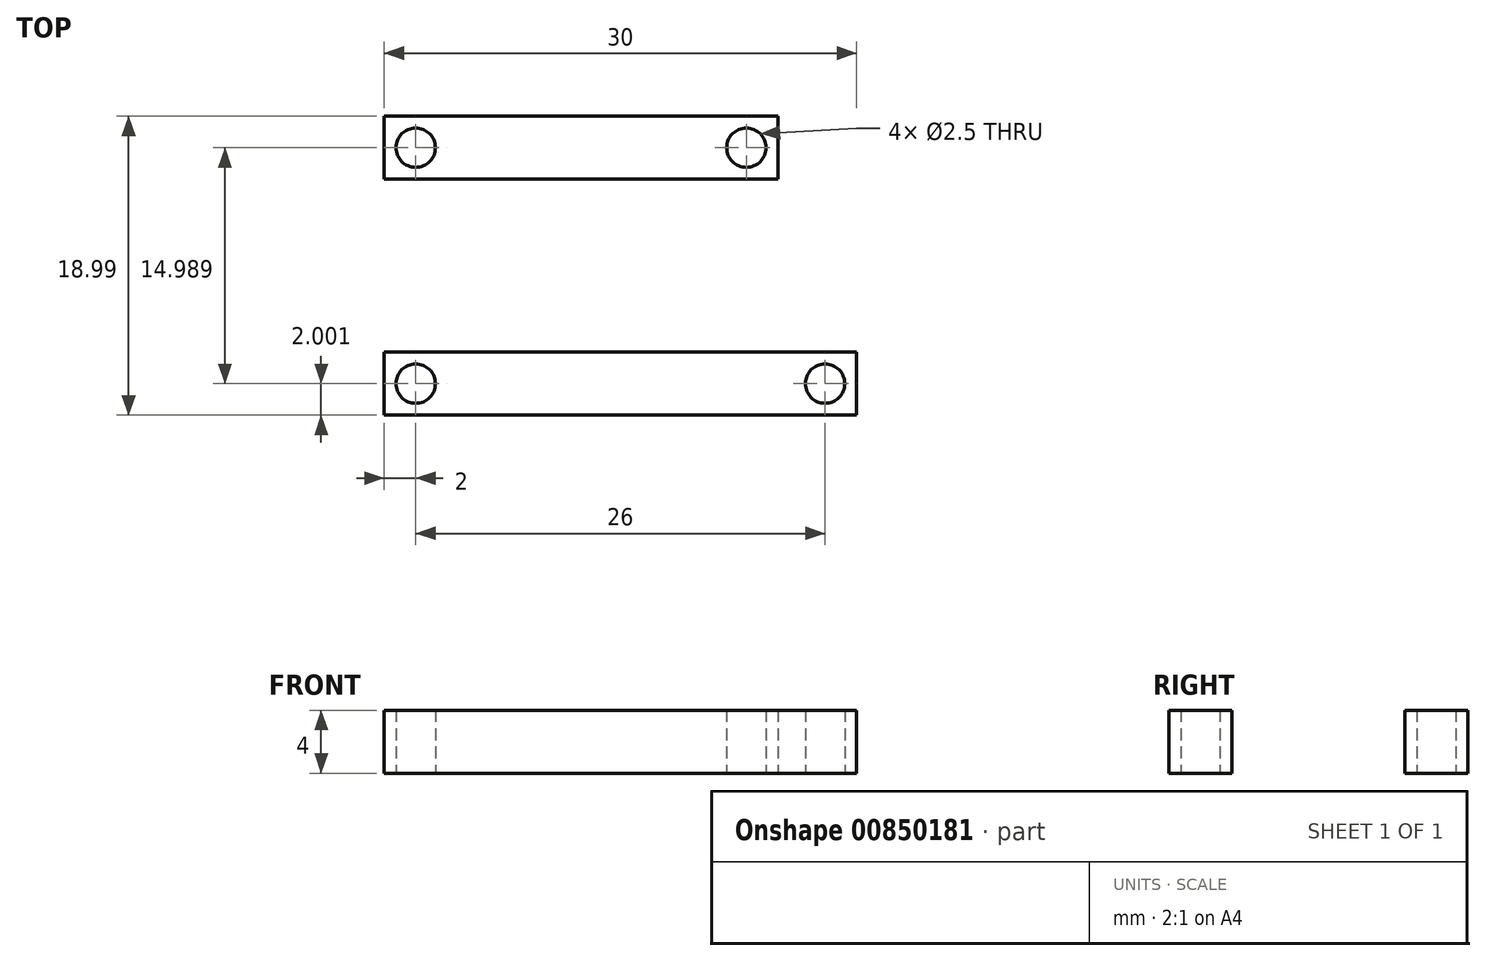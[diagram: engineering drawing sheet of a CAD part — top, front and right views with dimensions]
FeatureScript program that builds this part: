
annotation { "Feature Type Name" : "Feature", "Feature Type Description" : "" }
export const myFeature = defineFeature(function(context is Context, id is Id, definition is map)
    precondition{}
    {
        {
            var Q0;
            Q0=qCreatedBy(makeId("Top.planeOp"),FACE);
            var sketch = newSketch(context, id + "F0", { "sketchPlane" : qUnion([Q0])});
            skLineSegment(sketch, "E0.bottom", {"start": v(0, 0) * mm, "end": v(25, 0) * mm});
            skLineSegment(sketch, "E0.top", {"start": v(0, 4) * mm, "end": v(25, 4) * mm});
            skLineSegment(sketch, "E0.left", {"start": v(0, 0) * mm, "end": v(0, 4) * mm});
            skLineSegment(sketch, "E0.right", {"start": v(25, 0) * mm, "end": v(25, 4) * mm});
            skPoint(sketch, "E1", {"position": v(2, 2) * mm});
            skCircle(sketch, "E2", {"center": v(2, 2) * mm, "radius": 1.25 * mm});
            skPoint(sketch, "E3", {"position": v(23, 2) * mm});
            skCircle(sketch, "E4", {"center": v(23, 2) * mm, "radius": 1.25 * mm});
            skLineSegment(sketch, "E5.bottom", {"start": v(0, -14.99) * mm, "end": v(30, -14.99) * mm});
            skLineSegment(sketch, "E5.top", {"start": v(0, -10.99) * mm, "end": v(30, -10.99) * mm});
            skLineSegment(sketch, "E5.left", {"start": v(0, -14.99) * mm, "end": v(0, -10.99) * mm});
            skLineSegment(sketch, "E5.right", {"start": v(30, -14.99) * mm, "end": v(30, -10.99) * mm});
            skPoint(sketch, "E6", {"position": v(2, -12.99) * mm});
            skCircle(sketch, "E7", {"center": v(2, -12.99) * mm, "radius": 1.25 * mm});
            skPoint(sketch, "E8", {"position": v(28, -12.99) * mm});
            skCircle(sketch, "E9", {"center": v(28, -12.99) * mm, "radius": 1.25 * mm});
            skSolve(sketch);
        }
        {
            var Q0;
            Q0=makeQuery(id+"F0.imprint","IMPRINT",FACE,{"disambiguationData":[TD([[makeQuery(id+"F0.imprint","IMPRINT",EDGE,{"derivedFrom":sQuery(id+"F0.wireOp",EDGE,"E0.bottom")}),1.0]])]});
            extrude(context, id + "F1", {"entities" : qUnion([Q0]), "depth" : 4 * mm, "offsetDistance" : 25 * mm});
        }
        {
            var Q0;
            Q0=makeQuery(id+"F0.imprint","IMPRINT",FACE,{"disambiguationData":[TD([[makeQuery(id+"F0.imprint","IMPRINT",EDGE,{"derivedFrom":sQuery(id+"F0.wireOp",EDGE,"E5.bottom")}),1.0]])]});
            extrude(context, id + "F2", {"entities" : qUnion([Q0]), "depth" : 4 * mm, "offsetDistance" : 25 * mm});
        }
    });
